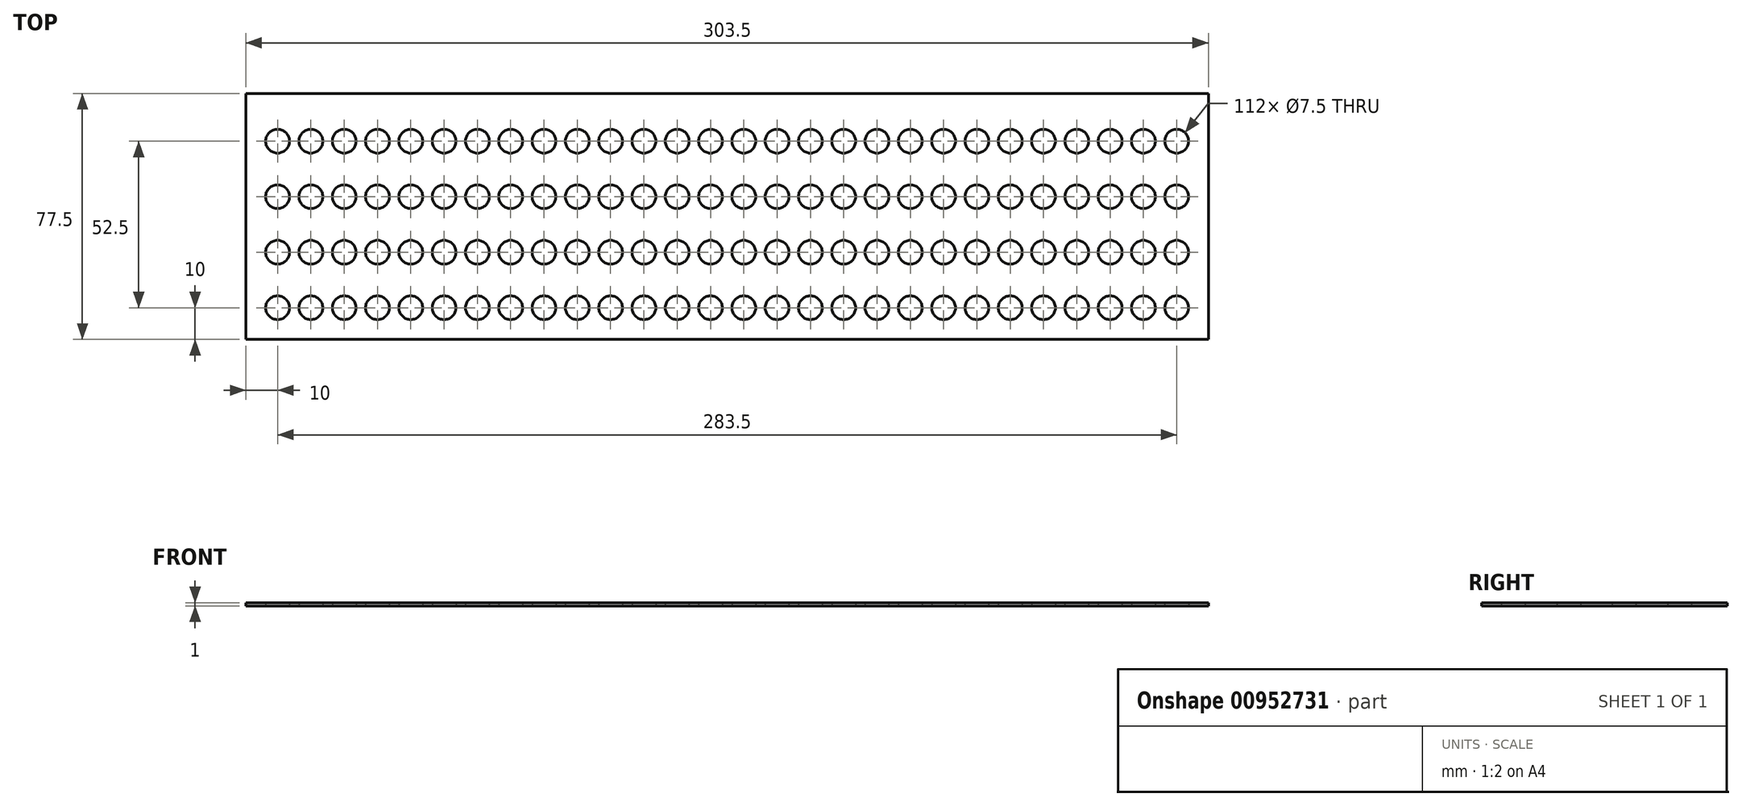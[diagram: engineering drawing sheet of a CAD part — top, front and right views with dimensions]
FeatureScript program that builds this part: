
annotation { "Feature Type Name" : "Feature", "Feature Type Description" : "" }
export const myFeature = defineFeature(function(context is Context, id is Id, definition is map)
    precondition{}
    {
        {
            var Q0;
            Q0=qCreatedBy(makeId("Top.planeOp"),FACE);
            var sketch = newSketch(context, id + "F0", { "sketchPlane" : qUnion([Q0])});
            skCircle(sketch, "E0", {"center": v(0, 0) * mm, "radius": 3.75 * mm});
            skCircle(sketch, "E1.0.1.0", {"center": v(0, 17.5) * mm, "radius": 3.75 * mm});
            skCircle(sketch, "E1.1.0.0", {"center": v(10.5, 0) * mm, "radius": 3.75 * mm});
            skCircle(sketch, "E1.1.1.0", {"center": v(10.5, 17.5) * mm, "radius": 3.75 * mm});
            skLineSegment(sketch, "E1.direction1", {"start": v(0, 0) * mm, "end": v(10.5, 0) * mm, "construction": true});
            skLineSegment(sketch, "E1.direction2", {"start": v(0, 0) * mm, "end": v(0, 17.5) * mm, "construction": true});
            skCircle(sketch, "E2.0.2.0", {"center": v(21, 0) * mm, "radius": 3.75 * mm});
            skCircle(sketch, "E2.0.2.1", {"center": v(21, 17.5) * mm, "radius": 3.75 * mm});
            skCircle(sketch, "E3.0.0.2", {"center": v(0, 35) * mm, "radius": 3.75 * mm});
            skCircle(sketch, "E3.0.1.2", {"center": v(10.5, 35) * mm, "radius": 3.75 * mm});
            skCircle(sketch, "E3.0.2.2", {"center": v(21, 35) * mm, "radius": 3.75 * mm});
            skCircle(sketch, "E4.0.3.0", {"center": v(31.5, 0) * mm, "radius": 3.75 * mm});
            skCircle(sketch, "E4.0.3.1", {"center": v(31.5, 17.5) * mm, "radius": 3.75 * mm});
            skCircle(sketch, "E4.0.3.2", {"center": v(31.5, 35) * mm, "radius": 3.75 * mm});
            skCircle(sketch, "E4.0.4.0", {"center": v(42, 0) * mm, "radius": 3.75 * mm});
            skCircle(sketch, "E4.0.4.1", {"center": v(42, 17.5) * mm, "radius": 3.75 * mm});
            skCircle(sketch, "E4.0.4.2", {"center": v(42, 35) * mm, "radius": 3.75 * mm});
            skCircle(sketch, "E4.0.5.0", {"center": v(52.5, 0) * mm, "radius": 3.75 * mm});
            skCircle(sketch, "E4.0.5.1", {"center": v(52.5, 17.5) * mm, "radius": 3.75 * mm});
            skCircle(sketch, "E4.0.5.2", {"center": v(52.5, 35) * mm, "radius": 3.75 * mm});
            skCircle(sketch, "E4.0.6.0", {"center": v(63, 0) * mm, "radius": 3.75 * mm});
            skCircle(sketch, "E4.0.6.1", {"center": v(63, 17.5) * mm, "radius": 3.75 * mm});
            skCircle(sketch, "E4.0.6.2", {"center": v(63, 35) * mm, "radius": 3.75 * mm});
            skCircle(sketch, "E4.0.7.0", {"center": v(73.5, 0) * mm, "radius": 3.75 * mm});
            skCircle(sketch, "E4.0.7.1", {"center": v(73.5, 17.5) * mm, "radius": 3.75 * mm});
            skCircle(sketch, "E4.0.7.2", {"center": v(73.5, 35) * mm, "radius": 3.75 * mm});
            skCircle(sketch, "E4.0.8.0", {"center": v(84, 0) * mm, "radius": 3.75 * mm});
            skCircle(sketch, "E4.0.8.1", {"center": v(84, 17.5) * mm, "radius": 3.75 * mm});
            skCircle(sketch, "E4.0.8.2", {"center": v(84, 35) * mm, "radius": 3.75 * mm});
            skCircle(sketch, "E4.0.9.0", {"center": v(94.5, 0) * mm, "radius": 3.75 * mm});
            skCircle(sketch, "E4.0.9.1", {"center": v(94.5, 17.5) * mm, "radius": 3.75 * mm});
            skCircle(sketch, "E4.0.9.2", {"center": v(94.5, 35) * mm, "radius": 3.75 * mm});
            skCircle(sketch, "E4.0.10.0", {"center": v(105, 0) * mm, "radius": 3.75 * mm});
            skCircle(sketch, "E4.0.10.1", {"center": v(105, 17.5) * mm, "radius": 3.75 * mm});
            skCircle(sketch, "E4.0.10.2", {"center": v(105, 35) * mm, "radius": 3.75 * mm});
            skCircle(sketch, "E4.0.11.0", {"center": v(115.5, 0) * mm, "radius": 3.75 * mm});
            skCircle(sketch, "E4.0.11.1", {"center": v(115.5, 17.5) * mm, "radius": 3.75 * mm});
            skCircle(sketch, "E4.0.11.2", {"center": v(115.5, 35) * mm, "radius": 3.75 * mm});
            skCircle(sketch, "E4.0.12.0", {"center": v(126, 0) * mm, "radius": 3.75 * mm});
            skCircle(sketch, "E4.0.12.1", {"center": v(126, 17.5) * mm, "radius": 3.75 * mm});
            skCircle(sketch, "E4.0.12.2", {"center": v(126, 35) * mm, "radius": 3.75 * mm});
            skCircle(sketch, "E4.0.13.0", {"center": v(136.5, 0) * mm, "radius": 3.75 * mm});
            skCircle(sketch, "E4.0.13.1", {"center": v(136.5, 17.5) * mm, "radius": 3.75 * mm});
            skCircle(sketch, "E4.0.13.2", {"center": v(136.5, 35) * mm, "radius": 3.75 * mm});
            skCircle(sketch, "E4.0.14.0", {"center": v(147, 0) * mm, "radius": 3.75 * mm});
            skCircle(sketch, "E4.0.14.1", {"center": v(147, 17.5) * mm, "radius": 3.75 * mm});
            skCircle(sketch, "E4.0.14.2", {"center": v(147, 35) * mm, "radius": 3.75 * mm});
            skCircle(sketch, "E4.0.15.0", {"center": v(157.5, 0) * mm, "radius": 3.75 * mm});
            skCircle(sketch, "E4.0.15.1", {"center": v(157.5, 17.5) * mm, "radius": 3.75 * mm});
            skCircle(sketch, "E4.0.15.2", {"center": v(157.5, 35) * mm, "radius": 3.75 * mm});
            skCircle(sketch, "E4.0.16.0", {"center": v(168, 0) * mm, "radius": 3.75 * mm});
            skCircle(sketch, "E4.0.16.1", {"center": v(168, 17.5) * mm, "radius": 3.75 * mm});
            skCircle(sketch, "E4.0.16.2", {"center": v(168, 35) * mm, "radius": 3.75 * mm});
            skCircle(sketch, "E4.0.17.0", {"center": v(178.5, 0) * mm, "radius": 3.75 * mm});
            skCircle(sketch, "E4.0.17.1", {"center": v(178.5, 17.5) * mm, "radius": 3.75 * mm});
            skCircle(sketch, "E4.0.17.2", {"center": v(178.5, 35) * mm, "radius": 3.75 * mm});
            skCircle(sketch, "E4.0.18.0", {"center": v(189, 0) * mm, "radius": 3.75 * mm});
            skCircle(sketch, "E4.0.18.1", {"center": v(189, 17.5) * mm, "radius": 3.75 * mm});
            skCircle(sketch, "E4.0.18.2", {"center": v(189, 35) * mm, "radius": 3.75 * mm});
            skCircle(sketch, "E4.0.19.0", {"center": v(199.5, 0) * mm, "radius": 3.75 * mm});
            skCircle(sketch, "E4.0.19.1", {"center": v(199.5, 17.5) * mm, "radius": 3.75 * mm});
            skCircle(sketch, "E4.0.19.2", {"center": v(199.5, 35) * mm, "radius": 3.75 * mm});
            skCircle(sketch, "E4.0.20.0", {"center": v(210, 0) * mm, "radius": 3.75 * mm});
            skCircle(sketch, "E4.0.20.1", {"center": v(210, 17.5) * mm, "radius": 3.75 * mm});
            skCircle(sketch, "E4.0.20.2", {"center": v(210, 35) * mm, "radius": 3.75 * mm});
            skCircle(sketch, "E4.0.21.0", {"center": v(220.5, 0) * mm, "radius": 3.75 * mm});
            skCircle(sketch, "E4.0.21.1", {"center": v(220.5, 17.5) * mm, "radius": 3.75 * mm});
            skCircle(sketch, "E4.0.21.2", {"center": v(220.5, 35) * mm, "radius": 3.75 * mm});
            skCircle(sketch, "E4.0.22.0", {"center": v(231, 0) * mm, "radius": 3.75 * mm});
            skCircle(sketch, "E4.0.22.1", {"center": v(231, 17.5) * mm, "radius": 3.75 * mm});
            skCircle(sketch, "E4.0.22.2", {"center": v(231, 35) * mm, "radius": 3.75 * mm});
            skCircle(sketch, "E4.0.23.0", {"center": v(241.5, 0) * mm, "radius": 3.75 * mm});
            skCircle(sketch, "E4.0.23.1", {"center": v(241.5, 17.5) * mm, "radius": 3.75 * mm});
            skCircle(sketch, "E4.0.23.2", {"center": v(241.5, 35) * mm, "radius": 3.75 * mm});
            skCircle(sketch, "E4.0.24.0", {"center": v(252, 0) * mm, "radius": 3.75 * mm});
            skCircle(sketch, "E4.0.24.1", {"center": v(252, 17.5) * mm, "radius": 3.75 * mm});
            skCircle(sketch, "E4.0.24.2", {"center": v(252, 35) * mm, "radius": 3.75 * mm});
            skCircle(sketch, "E5.0.25.0", {"center": v(262.5, 0) * mm, "radius": 3.75 * mm});
            skCircle(sketch, "E5.0.25.1", {"center": v(262.5, 17.5) * mm, "radius": 3.75 * mm});
            skCircle(sketch, "E5.0.25.2", {"center": v(262.5, 35) * mm, "radius": 3.75 * mm});
            skCircle(sketch, "E5.0.26.0", {"center": v(273, 0) * mm, "radius": 3.75 * mm});
            skCircle(sketch, "E5.0.26.1", {"center": v(273, 17.5) * mm, "radius": 3.75 * mm});
            skCircle(sketch, "E5.0.26.2", {"center": v(273, 35) * mm, "radius": 3.75 * mm});
            skCircle(sketch, "E5.0.27.0", {"center": v(283.5, 0) * mm, "radius": 3.75 * mm});
            skCircle(sketch, "E5.0.27.1", {"center": v(283.5, 17.5) * mm, "radius": 3.75 * mm});
            skCircle(sketch, "E5.0.27.2", {"center": v(283.5, 35) * mm, "radius": 3.75 * mm});
            skCircle(sketch, "E6.0.0.3", {"center": v(0, 52.5) * mm, "radius": 3.75 * mm});
            skCircle(sketch, "E6.0.1.3", {"center": v(10.5, 52.5) * mm, "radius": 3.75 * mm});
            skCircle(sketch, "E6.0.2.3", {"center": v(21, 52.5) * mm, "radius": 3.75 * mm});
            skCircle(sketch, "E6.0.3.3", {"center": v(31.5, 52.5) * mm, "radius": 3.75 * mm});
            skCircle(sketch, "E6.0.4.3", {"center": v(42, 52.5) * mm, "radius": 3.75 * mm});
            skCircle(sketch, "E6.0.5.3", {"center": v(52.5, 52.5) * mm, "radius": 3.75 * mm});
            skCircle(sketch, "E6.0.6.3", {"center": v(63, 52.5) * mm, "radius": 3.75 * mm});
            skCircle(sketch, "E6.0.7.3", {"center": v(73.5, 52.5) * mm, "radius": 3.75 * mm});
            skCircle(sketch, "E6.0.8.3", {"center": v(84, 52.5) * mm, "radius": 3.75 * mm});
            skCircle(sketch, "E6.0.9.3", {"center": v(94.5, 52.5) * mm, "radius": 3.75 * mm});
            skCircle(sketch, "E6.0.10.3", {"center": v(105, 52.5) * mm, "radius": 3.75 * mm});
            skCircle(sketch, "E6.0.11.3", {"center": v(115.5, 52.5) * mm, "radius": 3.75 * mm});
            skCircle(sketch, "E6.0.12.3", {"center": v(126, 52.5) * mm, "radius": 3.75 * mm});
            skCircle(sketch, "E6.0.13.3", {"center": v(136.5, 52.5) * mm, "radius": 3.75 * mm});
            skCircle(sketch, "E6.0.14.3", {"center": v(147, 52.5) * mm, "radius": 3.75 * mm});
            skCircle(sketch, "E6.0.15.3", {"center": v(157.5, 52.5) * mm, "radius": 3.75 * mm});
            skCircle(sketch, "E6.0.16.3", {"center": v(168, 52.5) * mm, "radius": 3.75 * mm});
            skCircle(sketch, "E6.0.17.3", {"center": v(178.5, 52.5) * mm, "radius": 3.75 * mm});
            skCircle(sketch, "E6.0.18.3", {"center": v(189, 52.5) * mm, "radius": 3.75 * mm});
            skCircle(sketch, "E6.0.19.3", {"center": v(199.5, 52.5) * mm, "radius": 3.75 * mm});
            skCircle(sketch, "E6.0.20.3", {"center": v(210, 52.5) * mm, "radius": 3.75 * mm});
            skCircle(sketch, "E6.0.21.3", {"center": v(220.5, 52.5) * mm, "radius": 3.75 * mm});
            skCircle(sketch, "E6.0.22.3", {"center": v(231, 52.5) * mm, "radius": 3.75 * mm});
            skCircle(sketch, "E6.0.23.3", {"center": v(241.5, 52.5) * mm, "radius": 3.75 * mm});
            skCircle(sketch, "E6.0.24.3", {"center": v(252, 52.5) * mm, "radius": 3.75 * mm});
            skCircle(sketch, "E6.0.25.3", {"center": v(262.5, 52.5) * mm, "radius": 3.75 * mm});
            skCircle(sketch, "E6.0.26.3", {"center": v(273, 52.5) * mm, "radius": 3.75 * mm});
            skCircle(sketch, "E6.0.27.3", {"center": v(283.5, 52.5) * mm, "radius": 3.75 * mm});
            skSolve(sketch);
        }
        {
            var Q0;
            Q0=qCreatedBy(makeId("Top.planeOp"),FACE);
            var sketch = newSketch(context, id + "F1", { "sketchPlane" : qUnion([Q0])});
            skLineSegment(sketch, "E7.bottom", {"start": v(-10, 67.5) * mm, "end": v(293.5, 67.5) * mm});
            skLineSegment(sketch, "E7.top", {"start": v(-10, -10) * mm, "end": v(293.5, -10) * mm});
            skLineSegment(sketch, "E7.left", {"start": v(-10, 67.5) * mm, "end": v(-10, -10) * mm});
            skLineSegment(sketch, "E7.right", {"start": v(293.5, 67.5) * mm, "end": v(293.5, -10) * mm});
            skSolve(sketch);
        }
        {
            var Q0;
            Q0=makeQuery(id+"F1.imprint","IMPRINT",FACE,{"disambiguationData":[TD([[makeQuery(id+"F1.imprint","IMPRINT",EDGE,{"derivedFrom":sQuery(id+"F1.wireOp",EDGE,"E7.bottom")}),-1.0]])]});
            extrude(context, id + "F2", {"entities" : qUnion([Q0]), "depth" : 1 * mm, "offsetDistance" : 25 * mm});
        }
        {
            var Q0;
            Q0=makeQuery(id+"F0.imprint","IMPRINT",FACE,{"disambiguationData":[TD([[makeQuery(id+"F0.imprint","IMPRINT",EDGE,{"derivedFrom":sQuery(id+"F0.wireOp",EDGE,"E4.0.11.1")}),1.0]])]});
            var Q1;
            Q1=makeQuery(id+"F0.imprint","IMPRINT",FACE,{"disambiguationData":[TD([[makeQuery(id+"F0.imprint","IMPRINT",EDGE,{"derivedFrom":sQuery(id+"F0.wireOp",EDGE,"E4.0.18.1")}),1.0]])]});
            var Q2;
            Q2=makeQuery(id+"F0.imprint","IMPRINT",FACE,{"disambiguationData":[TD([[makeQuery(id+"F0.imprint","IMPRINT",EDGE,{"derivedFrom":sQuery(id+"F0.wireOp",EDGE,"E4.0.8.0")}),1.0]])]});
            var Q3;
            Q3=makeQuery(id+"F0.imprint","IMPRINT",FACE,{"disambiguationData":[TD([[makeQuery(id+"F0.imprint","IMPRINT",EDGE,{"derivedFrom":sQuery(id+"F0.wireOp",EDGE,"E4.0.5.2")}),1.0]])]});
            var Q4;
            Q4=makeQuery(id+"F0.imprint","IMPRINT",FACE,{"disambiguationData":[TD([[makeQuery(id+"F0.imprint","IMPRINT",EDGE,{"derivedFrom":sQuery(id+"F0.wireOp",EDGE,"E3.0.0.2")}),1.0]])]});
            var Q5;
            Q5=makeQuery(id+"F0.imprint","IMPRINT",FACE,{"disambiguationData":[TD([[makeQuery(id+"F0.imprint","IMPRINT",EDGE,{"derivedFrom":sQuery(id+"F0.wireOp",EDGE,"E4.0.23.1")}),1.0]])]});
            var Q6;
            Q6=makeQuery(id+"F0.imprint","IMPRINT",FACE,{"disambiguationData":[TD([[makeQuery(id+"F0.imprint","IMPRINT",EDGE,{"derivedFrom":sQuery(id+"F0.wireOp",EDGE,"E4.0.13.0")}),1.0]])]});
            var Q7;
            Q7=makeQuery(id+"F0.imprint","IMPRINT",FACE,{"disambiguationData":[TD([[makeQuery(id+"F0.imprint","IMPRINT",EDGE,{"derivedFrom":sQuery(id+"F0.wireOp",EDGE,"E4.0.7.2")}),1.0]])]});
            var Q8;
            Q8=makeQuery(id+"F0.imprint","IMPRINT",FACE,{"disambiguationData":[TD([[makeQuery(id+"F0.imprint","IMPRINT",EDGE,{"derivedFrom":sQuery(id+"F0.wireOp",EDGE,"E4.0.19.0")}),1.0]])]});
            var Q9;
            Q9=makeQuery(id+"F0.imprint","IMPRINT",FACE,{"disambiguationData":[TD([[makeQuery(id+"F0.imprint","IMPRINT",EDGE,{"derivedFrom":sQuery(id+"F0.wireOp",EDGE,"E3.0.2.2")}),1.0]])]});
            var Q10;
            Q10=makeQuery(id+"F0.imprint","IMPRINT",FACE,{"disambiguationData":[TD([[makeQuery(id+"F0.imprint","IMPRINT",EDGE,{"derivedFrom":sQuery(id+"F0.wireOp",EDGE,"E4.0.8.1")}),1.0]])]});
            var Q11;
            Q11=makeQuery(id+"F0.imprint","IMPRINT",FACE,{"disambiguationData":[TD([[makeQuery(id+"F0.imprint","IMPRINT",EDGE,{"derivedFrom":sQuery(id+"F0.wireOp",EDGE,"E4.0.16.0")}),1.0]])]});
            var Q12;
            Q12=makeQuery(id+"F0.imprint","IMPRINT",FACE,{"disambiguationData":[TD([[makeQuery(id+"F0.imprint","IMPRINT",EDGE,{"derivedFrom":sQuery(id+"F0.wireOp",EDGE,"E4.0.16.2")}),1.0]])]});
            var Q13;
            Q13=makeQuery(id+"F0.imprint","IMPRINT",FACE,{"disambiguationData":[TD([[makeQuery(id+"F0.imprint","IMPRINT",EDGE,{"derivedFrom":sQuery(id+"F0.wireOp",EDGE,"E4.0.16.1")}),1.0]])]});
            var Q14;
            Q14=makeQuery(id+"F0.imprint","IMPRINT",FACE,{"disambiguationData":[TD([[makeQuery(id+"F0.imprint","IMPRINT",EDGE,{"derivedFrom":sQuery(id+"F0.wireOp",EDGE,"E4.0.6.0")}),1.0]])]});
            var Q15;
            Q15=makeQuery(id+"F0.imprint","IMPRINT",FACE,{"disambiguationData":[TD([[makeQuery(id+"F0.imprint","IMPRINT",EDGE,{"derivedFrom":sQuery(id+"F0.wireOp",EDGE,"E4.0.13.2")}),1.0]])]});
            var Q16;
            Q16=makeQuery(id+"F0.imprint","IMPRINT",FACE,{"disambiguationData":[TD([[makeQuery(id+"F0.imprint","IMPRINT",EDGE,{"derivedFrom":sQuery(id+"F0.wireOp",EDGE,"E4.0.24.1")}),1.0]])]});
            var Q17;
            Q17=makeQuery(id+"F0.imprint","IMPRINT",FACE,{"disambiguationData":[TD([[makeQuery(id+"F0.imprint","IMPRINT",EDGE,{"derivedFrom":sQuery(id+"F0.wireOp",EDGE,"E4.0.24.2")}),1.0]])]});
            var Q18;
            Q18=makeQuery(id+"F0.imprint","IMPRINT",FACE,{"disambiguationData":[TD([[makeQuery(id+"F0.imprint","IMPRINT",EDGE,{"derivedFrom":sQuery(id+"F0.wireOp",EDGE,"E4.0.15.1")}),1.0]])]});
            var Q19;
            Q19=makeQuery(id+"F0.imprint","IMPRINT",FACE,{"disambiguationData":[TD([[makeQuery(id+"F0.imprint","IMPRINT",EDGE,{"derivedFrom":sQuery(id+"F0.wireOp",EDGE,"E4.0.5.0")}),1.0]])]});
            var Q20;
            Q20=makeQuery(id+"F0.imprint","IMPRINT",FACE,{"disambiguationData":[TD([[makeQuery(id+"F0.imprint","IMPRINT",EDGE,{"derivedFrom":sQuery(id+"F0.wireOp",EDGE,"E4.0.4.1")}),1.0]])]});
            var Q21;
            Q21=makeQuery(id+"F0.imprint","IMPRINT",FACE,{"disambiguationData":[TD([[makeQuery(id+"F0.imprint","IMPRINT",EDGE,{"derivedFrom":sQuery(id+"F0.wireOp",EDGE,"E4.0.21.1")}),1.0]])]});
            var Q22;
            Q22=makeQuery(id+"F0.imprint","IMPRINT",FACE,{"disambiguationData":[TD([[makeQuery(id+"F0.imprint","IMPRINT",EDGE,{"derivedFrom":sQuery(id+"F0.wireOp",EDGE,"E4.0.9.0")}),1.0]])]});
            var Q23;
            Q23=makeQuery(id+"F0.imprint","IMPRINT",FACE,{"disambiguationData":[TD([[makeQuery(id+"F0.imprint","IMPRINT",EDGE,{"derivedFrom":sQuery(id+"F0.wireOp",EDGE,"E4.0.11.2")}),1.0]])]});
            var Q24;
            Q24=makeQuery(id+"F0.imprint","IMPRINT",FACE,{"disambiguationData":[TD([[makeQuery(id+"F0.imprint","IMPRINT",EDGE,{"derivedFrom":sQuery(id+"F0.wireOp",EDGE,"E4.0.12.1")}),1.0]])]});
            var Q25;
            Q25=makeQuery(id+"F0.imprint","IMPRINT",FACE,{"disambiguationData":[TD([[makeQuery(id+"F0.imprint","IMPRINT",EDGE,{"derivedFrom":sQuery(id+"F0.wireOp",EDGE,"E4.0.10.2")}),1.0]])]});
            var Q26;
            Q26=makeQuery(id+"F0.imprint","IMPRINT",FACE,{"disambiguationData":[TD([[makeQuery(id+"F0.imprint","IMPRINT",EDGE,{"derivedFrom":sQuery(id+"F0.wireOp",EDGE,"E4.0.17.1")}),1.0]])]});
            var Q27;
            Q27=makeQuery(id+"F0.imprint","IMPRINT",FACE,{"disambiguationData":[TD([[makeQuery(id+"F0.imprint","IMPRINT",EDGE,{"derivedFrom":sQuery(id+"F0.wireOp",EDGE,"E4.0.7.0")}),1.0]])]});
            var Q28;
            Q28=makeQuery(id+"F0.imprint","IMPRINT",FACE,{"disambiguationData":[TD([[makeQuery(id+"F0.imprint","IMPRINT",EDGE,{"derivedFrom":sQuery(id+"F0.wireOp",EDGE,"E4.0.20.2")}),1.0]])]});
            var Q29;
            Q29=makeQuery(id+"F0.imprint","IMPRINT",FACE,{"disambiguationData":[TD([[makeQuery(id+"F0.imprint","IMPRINT",EDGE,{"derivedFrom":sQuery(id+"F0.wireOp",EDGE,"E4.0.4.2")}),1.0]])]});
            var Q30;
            Q30=makeQuery(id+"F0.imprint","IMPRINT",FACE,{"disambiguationData":[TD([[makeQuery(id+"F0.imprint","IMPRINT",EDGE,{"derivedFrom":sQuery(id+"F0.wireOp",EDGE,"E4.0.3.1")}),1.0]])]});
            var Q31;
            Q31=makeQuery(id+"F0.imprint","IMPRINT",FACE,{"disambiguationData":[TD([[makeQuery(id+"F0.imprint","IMPRINT",EDGE,{"derivedFrom":sQuery(id+"F0.wireOp",EDGE,"E1.1.1.0")}),1.0]])]});
            var Q32;
            Q32=makeQuery(id+"F0.imprint","IMPRINT",FACE,{"disambiguationData":[TD([[makeQuery(id+"F0.imprint","IMPRINT",EDGE,{"derivedFrom":sQuery(id+"F0.wireOp",EDGE,"E4.0.14.1")}),1.0]])]});
            var Q33;
            Q33=makeQuery(id+"F0.imprint","IMPRINT",FACE,{"disambiguationData":[TD([[makeQuery(id+"F0.imprint","IMPRINT",EDGE,{"derivedFrom":sQuery(id+"F0.wireOp",EDGE,"E2.0.2.0")}),1.0]])]});
            var Q34;
            Q34=makeQuery(id+"F0.imprint","IMPRINT",FACE,{"disambiguationData":[TD([[makeQuery(id+"F0.imprint","IMPRINT",EDGE,{"derivedFrom":sQuery(id+"F0.wireOp",EDGE,"E4.0.7.1")}),1.0]])]});
            var Q35;
            Q35=makeQuery(id+"F0.imprint","IMPRINT",FACE,{"disambiguationData":[TD([[makeQuery(id+"F0.imprint","IMPRINT",EDGE,{"derivedFrom":sQuery(id+"F0.wireOp",EDGE,"E2.0.2.1")}),1.0]])]});
            var Q36;
            Q36=makeQuery(id+"F0.imprint","IMPRINT",FACE,{"disambiguationData":[TD([[makeQuery(id+"F0.imprint","IMPRINT",EDGE,{"derivedFrom":sQuery(id+"F0.wireOp",EDGE,"E4.0.11.0")}),1.0]])]});
            var Q37;
            Q37=makeQuery(id+"F0.imprint","IMPRINT",FACE,{"disambiguationData":[TD([[makeQuery(id+"F0.imprint","IMPRINT",EDGE,{"derivedFrom":sQuery(id+"F0.wireOp",EDGE,"E4.0.14.2")}),1.0]])]});
            var Q38;
            Q38=makeQuery(id+"F0.imprint","IMPRINT",FACE,{"disambiguationData":[TD([[makeQuery(id+"F0.imprint","IMPRINT",EDGE,{"derivedFrom":sQuery(id+"F0.wireOp",EDGE,"E4.0.19.1")}),1.0]])]});
            var Q39;
            Q39=makeQuery(id+"F0.imprint","IMPRINT",FACE,{"disambiguationData":[TD([[makeQuery(id+"F0.imprint","IMPRINT",EDGE,{"derivedFrom":sQuery(id+"F0.wireOp",EDGE,"E4.0.18.0")}),1.0]])]});
            var Q40;
            Q40=makeQuery(id+"F0.imprint","IMPRINT",FACE,{"disambiguationData":[TD([[makeQuery(id+"F0.imprint","IMPRINT",EDGE,{"derivedFrom":sQuery(id+"F0.wireOp",EDGE,"E4.0.20.1")}),1.0]])]});
            var Q41;
            Q41=makeQuery(id+"F0.imprint","IMPRINT",FACE,{"disambiguationData":[TD([[makeQuery(id+"F0.imprint","IMPRINT",EDGE,{"derivedFrom":sQuery(id+"F0.wireOp",EDGE,"E4.0.9.2")}),1.0]])]});
            var Q42;
            Q42=makeQuery(id+"F0.imprint","IMPRINT",FACE,{"disambiguationData":[TD([[makeQuery(id+"F0.imprint","IMPRINT",EDGE,{"derivedFrom":sQuery(id+"F0.wireOp",EDGE,"E4.0.12.2")}),1.0]])]});
            var Q43;
            Q43=makeQuery(id+"F0.imprint","IMPRINT",FACE,{"disambiguationData":[TD([[makeQuery(id+"F0.imprint","IMPRINT",EDGE,{"derivedFrom":sQuery(id+"F0.wireOp",EDGE,"E4.0.8.2")}),1.0]])]});
            var Q44;
            Q44=makeQuery(id+"F0.imprint","IMPRINT",FACE,{"disambiguationData":[TD([[makeQuery(id+"F0.imprint","IMPRINT",EDGE,{"derivedFrom":sQuery(id+"F0.wireOp",EDGE,"E4.0.10.0")}),1.0]])]});
            var Q45;
            Q45=makeQuery(id+"F0.imprint","IMPRINT",FACE,{"disambiguationData":[TD([[makeQuery(id+"F0.imprint","IMPRINT",EDGE,{"derivedFrom":sQuery(id+"F0.wireOp",EDGE,"E4.0.21.2")}),1.0]])]});
            var Q46;
            Q46=makeQuery(id+"F0.imprint","IMPRINT",FACE,{"disambiguationData":[TD([[makeQuery(id+"F0.imprint","IMPRINT",EDGE,{"derivedFrom":sQuery(id+"F0.wireOp",EDGE,"E4.0.24.0")}),1.0]])]});
            var Q47;
            Q47=makeQuery(id+"F0.imprint","IMPRINT",FACE,{"disambiguationData":[TD([[makeQuery(id+"F0.imprint","IMPRINT",EDGE,{"derivedFrom":sQuery(id+"F0.wireOp",EDGE,"E4.0.15.2")}),1.0]])]});
            var Q48;
            Q48=makeQuery(id+"F0.imprint","IMPRINT",FACE,{"disambiguationData":[TD([[makeQuery(id+"F0.imprint","IMPRINT",EDGE,{"derivedFrom":sQuery(id+"F0.wireOp",EDGE,"E4.0.6.1")}),1.0]])]});
            var Q49;
            Q49=makeQuery(id+"F0.imprint","IMPRINT",FACE,{"disambiguationData":[TD([[makeQuery(id+"F0.imprint","IMPRINT",EDGE,{"derivedFrom":sQuery(id+"F0.wireOp",EDGE,"E4.0.3.0")}),1.0]])]});
            var Q50;
            Q50=makeQuery(id+"F0.imprint","IMPRINT",FACE,{"disambiguationData":[TD([[makeQuery(id+"F0.imprint","IMPRINT",EDGE,{"derivedFrom":sQuery(id+"F0.wireOp",EDGE,"E4.0.6.2")}),1.0]])]});
            var Q51;
            Q51=makeQuery(id+"F0.imprint","IMPRINT",FACE,{"disambiguationData":[TD([[makeQuery(id+"F0.imprint","IMPRINT",EDGE,{"derivedFrom":sQuery(id+"F0.wireOp",EDGE,"E4.0.17.2")}),1.0]])]});
            var Q52;
            Q52=makeQuery(id+"F0.imprint","IMPRINT",FACE,{"disambiguationData":[TD([[makeQuery(id+"F0.imprint","IMPRINT",EDGE,{"derivedFrom":sQuery(id+"F0.wireOp",EDGE,"E4.0.23.0")}),1.0]])]});
            var Q53;
            Q53=makeQuery(id+"F0.imprint","IMPRINT",FACE,{"disambiguationData":[TD([[makeQuery(id+"F0.imprint","IMPRINT",EDGE,{"derivedFrom":sQuery(id+"F0.wireOp",EDGE,"E4.0.20.0")}),1.0]])]});
            var Q54;
            Q54=makeQuery(id+"F0.imprint","IMPRINT",FACE,{"disambiguationData":[TD([[makeQuery(id+"F0.imprint","IMPRINT",EDGE,{"derivedFrom":sQuery(id+"F0.wireOp",EDGE,"E4.0.13.1")}),1.0]])]});
            var Q55;
            Q55=makeQuery(id+"F0.imprint","IMPRINT",FACE,{"disambiguationData":[TD([[makeQuery(id+"F0.imprint","IMPRINT",EDGE,{"derivedFrom":sQuery(id+"F0.wireOp",EDGE,"E4.0.22.1")}),1.0]])]});
            var Q56;
            Q56=makeQuery(id+"F0.imprint","IMPRINT",FACE,{"disambiguationData":[TD([[makeQuery(id+"F0.imprint","IMPRINT",EDGE,{"derivedFrom":sQuery(id+"F0.wireOp",EDGE,"E4.0.5.1")}),1.0]])]});
            var Q57;
            Q57=makeQuery(id+"F0.imprint","IMPRINT",FACE,{"disambiguationData":[TD([[makeQuery(id+"F0.imprint","IMPRINT",EDGE,{"derivedFrom":sQuery(id+"F0.wireOp",EDGE,"E4.0.17.0")}),1.0]])]});
            var Q58;
            Q58=makeQuery(id+"F0.imprint","IMPRINT",FACE,{"disambiguationData":[TD([[makeQuery(id+"F0.imprint","IMPRINT",EDGE,{"derivedFrom":sQuery(id+"F0.wireOp",EDGE,"E4.0.21.0")}),1.0]])]});
            var Q59;
            Q59=makeQuery(id+"F0.imprint","IMPRINT",FACE,{"disambiguationData":[TD([[makeQuery(id+"F0.imprint","IMPRINT",EDGE,{"derivedFrom":sQuery(id+"F0.wireOp",EDGE,"E4.0.18.2")}),1.0]])]});
            var Q60;
            Q60=makeQuery(id+"F0.imprint","IMPRINT",FACE,{"disambiguationData":[TD([[makeQuery(id+"F0.imprint","IMPRINT",EDGE,{"derivedFrom":sQuery(id+"F0.wireOp",EDGE,"E4.0.14.0")}),1.0]])]});
            var Q61;
            Q61=makeQuery(id+"F0.imprint","IMPRINT",FACE,{"disambiguationData":[TD([[makeQuery(id+"F0.imprint","IMPRINT",EDGE,{"derivedFrom":sQuery(id+"F0.wireOp",EDGE,"E4.0.9.1")}),1.0]])]});
            var Q62;
            Q62=makeQuery(id+"F0.imprint","IMPRINT",FACE,{"disambiguationData":[TD([[makeQuery(id+"F0.imprint","IMPRINT",EDGE,{"derivedFrom":sQuery(id+"F0.wireOp",EDGE,"E4.0.10.1")}),1.0]])]});
            var Q63;
            Q63=makeQuery(id+"F0.imprint","IMPRINT",FACE,{"disambiguationData":[TD([[makeQuery(id+"F0.imprint","IMPRINT",EDGE,{"derivedFrom":sQuery(id+"F0.wireOp",EDGE,"E3.0.1.2")}),1.0]])]});
            var Q64;
            Q64=makeQuery(id+"F0.imprint","IMPRINT",FACE,{"disambiguationData":[TD([[makeQuery(id+"F0.imprint","IMPRINT",EDGE,{"derivedFrom":sQuery(id+"F0.wireOp",EDGE,"E4.0.22.0")}),1.0]])]});
            var Q65;
            Q65=makeQuery(id+"F0.imprint","IMPRINT",FACE,{"disambiguationData":[TD([[makeQuery(id+"F0.imprint","IMPRINT",EDGE,{"derivedFrom":sQuery(id+"F0.wireOp",EDGE,"E4.0.3.2")}),1.0]])]});
            var Q66;
            Q66=makeQuery(id+"F0.imprint","IMPRINT",FACE,{"disambiguationData":[TD([[makeQuery(id+"F0.imprint","IMPRINT",EDGE,{"derivedFrom":sQuery(id+"F0.wireOp",EDGE,"E4.0.22.2")}),1.0]])]});
            var Q67;
            Q67=makeQuery(id+"F0.imprint","IMPRINT",FACE,{"disambiguationData":[TD([[makeQuery(id+"F0.imprint","IMPRINT",EDGE,{"derivedFrom":sQuery(id+"F0.wireOp",EDGE,"E4.0.23.2")}),1.0]])]});
            var Q68;
            Q68=makeQuery(id+"F0.imprint","IMPRINT",FACE,{"disambiguationData":[TD([[makeQuery(id+"F0.imprint","IMPRINT",EDGE,{"derivedFrom":sQuery(id+"F0.wireOp",EDGE,"E4.0.15.0")}),1.0]])]});
            var Q69;
            Q69=makeQuery(id+"F0.imprint","IMPRINT",FACE,{"disambiguationData":[TD([[makeQuery(id+"F0.imprint","IMPRINT",EDGE,{"derivedFrom":sQuery(id+"F0.wireOp",EDGE,"E4.0.12.0")}),1.0]])]});
            var Q70;
            Q70=makeQuery(id+"F0.imprint","IMPRINT",FACE,{"disambiguationData":[TD([[makeQuery(id+"F0.imprint","IMPRINT",EDGE,{"derivedFrom":sQuery(id+"F0.wireOp",EDGE,"E4.0.4.0")}),1.0]])]});
            var Q71;
            Q71=makeQuery(id+"F0.imprint","IMPRINT",FACE,{"disambiguationData":[TD([[makeQuery(id+"F0.imprint","IMPRINT",EDGE,{"derivedFrom":sQuery(id+"F0.wireOp",EDGE,"E1.1.0.0")}),1.0]])]});
            var Q72;
            Q72=makeQuery(id+"F0.imprint","IMPRINT",FACE,{"disambiguationData":[TD([[makeQuery(id+"F0.imprint","IMPRINT",EDGE,{"derivedFrom":sQuery(id+"F0.wireOp",EDGE,"E4.0.19.2")}),1.0]])]});
            var Q73;
            Q73=makeQuery(id+"F0.imprint","IMPRINT",FACE,{"disambiguationData":[TD([[makeQuery(id+"F0.imprint","IMPRINT",EDGE,{"derivedFrom":sQuery(id+"F0.wireOp",EDGE,"E1.0.1.0")}),1.0]])]});
            var Q74;
            Q74=makeQuery(id+"F0.imprint","IMPRINT",FACE,{"disambiguationData":[TD([[makeQuery(id+"F0.imprint","IMPRINT",EDGE,{"derivedFrom":sQuery(id+"F0.wireOp",EDGE,"E0")}),1.0]])]});
            var Q75;
            Q75=makeQuery(id+"F0.imprint","IMPRINT",FACE,{"disambiguationData":[TD([[makeQuery(id+"F0.imprint","IMPRINT",EDGE,{"derivedFrom":sQuery(id+"F0.wireOp",EDGE,"E5.0.25.2")}),1.0]])]});
            var Q76;
            Q76=makeQuery(id+"F0.imprint","IMPRINT",FACE,{"disambiguationData":[TD([[makeQuery(id+"F0.imprint","IMPRINT",EDGE,{"derivedFrom":sQuery(id+"F0.wireOp",EDGE,"E5.0.26.2")}),1.0]])]});
            var Q77;
            Q77=makeQuery(id+"F0.imprint","IMPRINT",FACE,{"disambiguationData":[TD([[makeQuery(id+"F0.imprint","IMPRINT",EDGE,{"derivedFrom":sQuery(id+"F0.wireOp",EDGE,"E5.0.27.2")}),1.0]])]});
            var Q78;
            Q78=makeQuery(id+"F0.imprint","IMPRINT",FACE,{"disambiguationData":[TD([[makeQuery(id+"F0.imprint","IMPRINT",EDGE,{"derivedFrom":sQuery(id+"F0.wireOp",EDGE,"E5.0.27.1")}),1.0]])]});
            var Q79;
            Q79=makeQuery(id+"F0.imprint","IMPRINT",FACE,{"disambiguationData":[TD([[makeQuery(id+"F0.imprint","IMPRINT",EDGE,{"derivedFrom":sQuery(id+"F0.wireOp",EDGE,"E5.0.26.1")}),1.0]])]});
            var Q80;
            Q80=makeQuery(id+"F0.imprint","IMPRINT",FACE,{"disambiguationData":[TD([[makeQuery(id+"F0.imprint","IMPRINT",EDGE,{"derivedFrom":sQuery(id+"F0.wireOp",EDGE,"E5.0.25.1")}),1.0]])]});
            var Q81;
            Q81=makeQuery(id+"F0.imprint","IMPRINT",FACE,{"disambiguationData":[TD([[makeQuery(id+"F0.imprint","IMPRINT",EDGE,{"derivedFrom":sQuery(id+"F0.wireOp",EDGE,"E5.0.25.0")}),1.0]])]});
            var Q82;
            Q82=makeQuery(id+"F0.imprint","IMPRINT",FACE,{"disambiguationData":[TD([[makeQuery(id+"F0.imprint","IMPRINT",EDGE,{"derivedFrom":sQuery(id+"F0.wireOp",EDGE,"E5.0.26.0")}),1.0]])]});
            var Q83;
            Q83=makeQuery(id+"F0.imprint","IMPRINT",FACE,{"disambiguationData":[TD([[makeQuery(id+"F0.imprint","IMPRINT",EDGE,{"derivedFrom":sQuery(id+"F0.wireOp",EDGE,"E5.0.27.0")}),1.0]])]});
            var Q84;
            Q84=makeQuery(id+"F0.imprint","IMPRINT",FACE,{"disambiguationData":[TD([[makeQuery(id+"F0.imprint","IMPRINT",EDGE,{"derivedFrom":sQuery(id+"F0.wireOp",EDGE,"E6.0.6.3")}),1.0]])]});
            var Q85;
            Q85=makeQuery(id+"F0.imprint","IMPRINT",FACE,{"disambiguationData":[TD([[makeQuery(id+"F0.imprint","IMPRINT",EDGE,{"derivedFrom":sQuery(id+"F0.wireOp",EDGE,"E6.0.9.3")}),1.0]])]});
            var Q86;
            Q86=makeQuery(id+"F0.imprint","IMPRINT",FACE,{"disambiguationData":[TD([[makeQuery(id+"F0.imprint","IMPRINT",EDGE,{"derivedFrom":sQuery(id+"F0.wireOp",EDGE,"E6.0.1.3")}),1.0]])]});
            var Q87;
            Q87=makeQuery(id+"F0.imprint","IMPRINT",FACE,{"disambiguationData":[TD([[makeQuery(id+"F0.imprint","IMPRINT",EDGE,{"derivedFrom":sQuery(id+"F0.wireOp",EDGE,"E6.0.16.3")}),1.0]])]});
            var Q88;
            Q88=makeQuery(id+"F0.imprint","IMPRINT",FACE,{"disambiguationData":[TD([[makeQuery(id+"F0.imprint","IMPRINT",EDGE,{"derivedFrom":sQuery(id+"F0.wireOp",EDGE,"E6.0.7.3")}),1.0]])]});
            var Q89;
            Q89=makeQuery(id+"F0.imprint","IMPRINT",FACE,{"disambiguationData":[TD([[makeQuery(id+"F0.imprint","IMPRINT",EDGE,{"derivedFrom":sQuery(id+"F0.wireOp",EDGE,"E6.0.3.3")}),1.0]])]});
            var Q90;
            Q90=makeQuery(id+"F0.imprint","IMPRINT",FACE,{"disambiguationData":[TD([[makeQuery(id+"F0.imprint","IMPRINT",EDGE,{"derivedFrom":sQuery(id+"F0.wireOp",EDGE,"E6.0.12.3")}),1.0]])]});
            var Q91;
            Q91=makeQuery(id+"F0.imprint","IMPRINT",FACE,{"disambiguationData":[TD([[makeQuery(id+"F0.imprint","IMPRINT",EDGE,{"derivedFrom":sQuery(id+"F0.wireOp",EDGE,"E6.0.2.3")}),1.0]])]});
            var Q92;
            Q92=makeQuery(id+"F0.imprint","IMPRINT",FACE,{"disambiguationData":[TD([[makeQuery(id+"F0.imprint","IMPRINT",EDGE,{"derivedFrom":sQuery(id+"F0.wireOp",EDGE,"E6.0.10.3")}),1.0]])]});
            var Q93;
            Q93=makeQuery(id+"F0.imprint","IMPRINT",FACE,{"disambiguationData":[TD([[makeQuery(id+"F0.imprint","IMPRINT",EDGE,{"derivedFrom":sQuery(id+"F0.wireOp",EDGE,"E6.0.11.3")}),1.0]])]});
            var Q94;
            Q94=makeQuery(id+"F0.imprint","IMPRINT",FACE,{"disambiguationData":[TD([[makeQuery(id+"F0.imprint","IMPRINT",EDGE,{"derivedFrom":sQuery(id+"F0.wireOp",EDGE,"E6.0.15.3")}),1.0]])]});
            var Q95;
            Q95=makeQuery(id+"F0.imprint","IMPRINT",FACE,{"disambiguationData":[TD([[makeQuery(id+"F0.imprint","IMPRINT",EDGE,{"derivedFrom":sQuery(id+"F0.wireOp",EDGE,"E6.0.4.3")}),1.0]])]});
            var Q96;
            Q96=makeQuery(id+"F0.imprint","IMPRINT",FACE,{"disambiguationData":[TD([[makeQuery(id+"F0.imprint","IMPRINT",EDGE,{"derivedFrom":sQuery(id+"F0.wireOp",EDGE,"E6.0.5.3")}),1.0]])]});
            var Q97;
            Q97=makeQuery(id+"F0.imprint","IMPRINT",FACE,{"disambiguationData":[TD([[makeQuery(id+"F0.imprint","IMPRINT",EDGE,{"derivedFrom":sQuery(id+"F0.wireOp",EDGE,"E6.0.14.3")}),1.0]])]});
            var Q98;
            Q98=makeQuery(id+"F0.imprint","IMPRINT",FACE,{"disambiguationData":[TD([[makeQuery(id+"F0.imprint","IMPRINT",EDGE,{"derivedFrom":sQuery(id+"F0.wireOp",EDGE,"E6.0.13.3")}),1.0]])]});
            var Q99;
            Q99=makeQuery(id+"F0.imprint","IMPRINT",FACE,{"disambiguationData":[TD([[makeQuery(id+"F0.imprint","IMPRINT",EDGE,{"derivedFrom":sQuery(id+"F0.wireOp",EDGE,"E6.0.8.3")}),1.0]])]});
            var Q100;
            Q100=makeQuery(id+"F0.imprint","IMPRINT",FACE,{"disambiguationData":[TD([[makeQuery(id+"F0.imprint","IMPRINT",EDGE,{"derivedFrom":sQuery(id+"F0.wireOp",EDGE,"E6.0.0.3")}),1.0]])]});
            var Q101;
            Q101=makeQuery(id+"F0.imprint","IMPRINT",FACE,{"disambiguationData":[TD([[makeQuery(id+"F0.imprint","IMPRINT",EDGE,{"derivedFrom":sQuery(id+"F0.wireOp",EDGE,"E6.0.27.3")}),1.0]])]});
            var Q102;
            Q102=makeQuery(id+"F0.imprint","IMPRINT",FACE,{"disambiguationData":[TD([[makeQuery(id+"F0.imprint","IMPRINT",EDGE,{"derivedFrom":sQuery(id+"F0.wireOp",EDGE,"E6.0.20.3")}),1.0]])]});
            var Q103;
            Q103=makeQuery(id+"F0.imprint","IMPRINT",FACE,{"disambiguationData":[TD([[makeQuery(id+"F0.imprint","IMPRINT",EDGE,{"derivedFrom":sQuery(id+"F0.wireOp",EDGE,"E6.0.22.3")}),1.0]])]});
            var Q104;
            Q104=makeQuery(id+"F0.imprint","IMPRINT",FACE,{"disambiguationData":[TD([[makeQuery(id+"F0.imprint","IMPRINT",EDGE,{"derivedFrom":sQuery(id+"F0.wireOp",EDGE,"E6.0.21.3")}),1.0]])]});
            var Q105;
            Q105=makeQuery(id+"F0.imprint","IMPRINT",FACE,{"disambiguationData":[TD([[makeQuery(id+"F0.imprint","IMPRINT",EDGE,{"derivedFrom":sQuery(id+"F0.wireOp",EDGE,"E6.0.26.3")}),1.0]])]});
            var Q106;
            Q106=makeQuery(id+"F0.imprint","IMPRINT",FACE,{"disambiguationData":[TD([[makeQuery(id+"F0.imprint","IMPRINT",EDGE,{"derivedFrom":sQuery(id+"F0.wireOp",EDGE,"E6.0.25.3")}),1.0]])]});
            var Q107;
            Q107=makeQuery(id+"F0.imprint","IMPRINT",FACE,{"disambiguationData":[TD([[makeQuery(id+"F0.imprint","IMPRINT",EDGE,{"derivedFrom":sQuery(id+"F0.wireOp",EDGE,"E6.0.17.3")}),1.0]])]});
            var Q108;
            Q108=makeQuery(id+"F0.imprint","IMPRINT",FACE,{"disambiguationData":[TD([[makeQuery(id+"F0.imprint","IMPRINT",EDGE,{"derivedFrom":sQuery(id+"F0.wireOp",EDGE,"E6.0.18.3")}),1.0]])]});
            var Q109;
            Q109=makeQuery(id+"F0.imprint","IMPRINT",FACE,{"disambiguationData":[TD([[makeQuery(id+"F0.imprint","IMPRINT",EDGE,{"derivedFrom":sQuery(id+"F0.wireOp",EDGE,"E6.0.19.3")}),1.0]])]});
            var Q110;
            Q110=makeQuery(id+"F0.imprint","IMPRINT",FACE,{"disambiguationData":[TD([[makeQuery(id+"F0.imprint","IMPRINT",EDGE,{"derivedFrom":sQuery(id+"F0.wireOp",EDGE,"E6.0.23.3")}),1.0]])]});
            var Q111;
            Q111=makeQuery(id+"F0.imprint","IMPRINT",FACE,{"disambiguationData":[TD([[makeQuery(id+"F0.imprint","IMPRINT",EDGE,{"derivedFrom":sQuery(id+"F0.wireOp",EDGE,"E6.0.24.3")}),1.0]])]});
            extrude(context, id + "F3", {"entities" : qUnion([Q0, Q1, Q2, Q3, Q4, Q5, Q6, Q7, Q8, Q9, Q10, Q11, Q12, Q13, Q14, Q15, Q16, Q17, Q18, Q19, Q20, Q21, Q22, Q23, Q24, Q25, Q26, Q27, Q28, Q29, Q30, Q31, Q32, Q33, Q34, Q35, Q36, Q37, Q38, Q39, Q40, Q41, Q42, Q43, Q44, Q45, Q46, Q47, Q48, Q49, Q50, Q51, Q52, Q53, Q54, Q55, Q56, Q57, Q58, Q59, Q60, Q61, Q62, Q63, Q64, Q65, Q66, Q67, Q68, Q69, Q70, Q71, Q72, Q73, Q74, Q75, Q76, Q77, Q78, Q79, Q80, Q81, Q82, Q83, Q84, Q85, Q86, Q87, Q88, Q89, Q90, Q91, Q92, Q93, Q94, Q95, Q96, Q97, Q98, Q99, Q100, Q101, Q102, Q103, Q104, Q105, Q106, Q107, Q108, Q109, Q110, Q111]), "operationType" : NewBodyOperationType.REMOVE, "depth" : 25 * mm, "offsetDistance" : 25 * mm});
        }
    });
